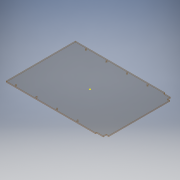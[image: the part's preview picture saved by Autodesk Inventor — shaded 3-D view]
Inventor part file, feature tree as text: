
AUTODESK INVENTOR PART (.ipt)
format: ipt  version: 2019.4 (Build 234330000, 330)  size: 156,672 bytes
history: native  units: mm
features: sketch x5, extrude x3
ambient origin geometry x8: Origin, YZ Plane, XZ Plane, XY Plane, X Axis, Y Axis, Z Axis, Center Point
bodies: Solid1 (feature_tree)
feature tree (8):
  extrude  "Extrusion1"  Depth=337.83mm
  extrude  "Extrusion2"  Depth=20.0mm
  extrude  "Extrusion3"  Depth=5.0mm
  sketch  "Sketch5"  dims[d7=90.0deg]
  sketch  "Sketch6"  dims[d8=15.0mm d9=32.0mm d10=5.0mm d11=0.0mm d14=40.0mm d15=8.732mm d16=5.5mm d17=40.0mm d19=100.0mm d20=10.0mm d22=10.0mm d24=60.0mm d25=8.732mm d26=5.5mm d27=40.0mm d29=100.0mm d30=10.0mm d32=10.0mm d34=10.0mm d35=0.0mm d36=480.0mm d37=339.0mm]
  sketch  "Sketch1"  dims[d0=480.0mm d1=337.83mm]
  sketch  "Sketch2"  dims[d2=5.0mm d3=0.0mm d4=20.0mm]
  sketch  "Sketch4"  dims[d5=12.0mm d6=5.0mm]
